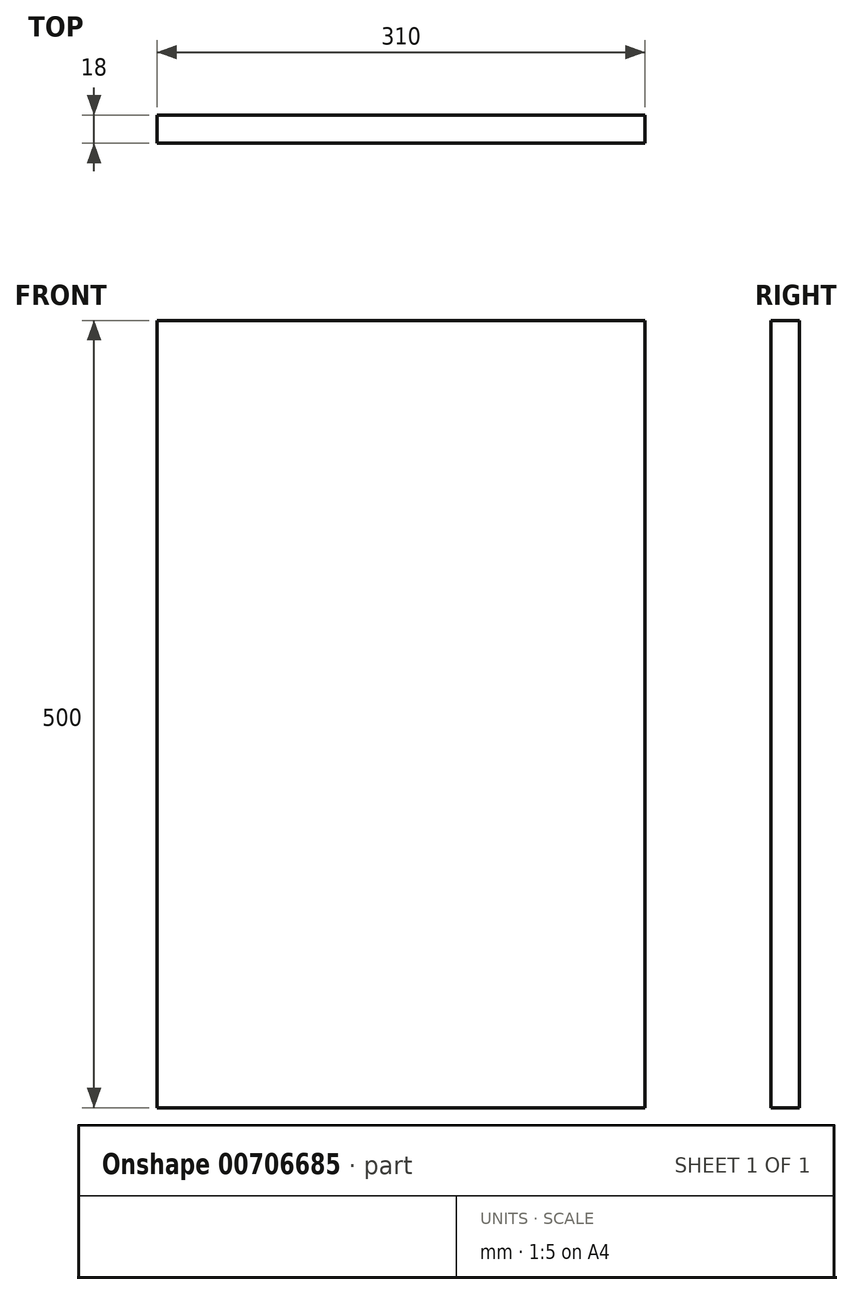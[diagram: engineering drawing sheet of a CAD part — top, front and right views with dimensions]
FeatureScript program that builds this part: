
annotation { "Feature Type Name" : "Feature", "Feature Type Description" : "" }
export const myFeature = defineFeature(function(context is Context, id is Id, definition is map)
    precondition{}
    {
        {
            var Q0;
            Q0=qCreatedBy(makeId("Front.planeOp"),FACE);
            var sketch = newSketch(context, id + "F0", { "sketchPlane" : qUnion([Q0])});
            skLineSegment(sketch, "E0.bottom", {"start": v(-155, -250) * mm, "end": v(155, -250) * mm});
            skLineSegment(sketch, "E0.top", {"start": v(-155, 250) * mm, "end": v(155, 250) * mm});
            skLineSegment(sketch, "E0.left", {"start": v(-155, -250) * mm, "end": v(-155, 250) * mm});
            skLineSegment(sketch, "E0.right", {"start": v(155, -250) * mm, "end": v(155, 250) * mm});
            skPoint(sketch, "E0.middle", {"position": v(0, 0) * mm});
            skSolve(sketch);
        }
        {
            var Q0;
            Q0=makeQuery(id+"F0.imprint","IMPRINT",FACE,{"disambiguationData":[TD([[makeQuery(id+"F0.imprint","IMPRINT",EDGE,{"derivedFrom":sQuery(id+"F0.wireOp",EDGE,"E0.bottom")}),1.0]])]});
            extrude(context, id + "F1", {"entities" : qUnion([Q0]), "depth" : 18 * mm, "offsetDistance" : 25 * mm, "symmetric" : true});
        }
    });
